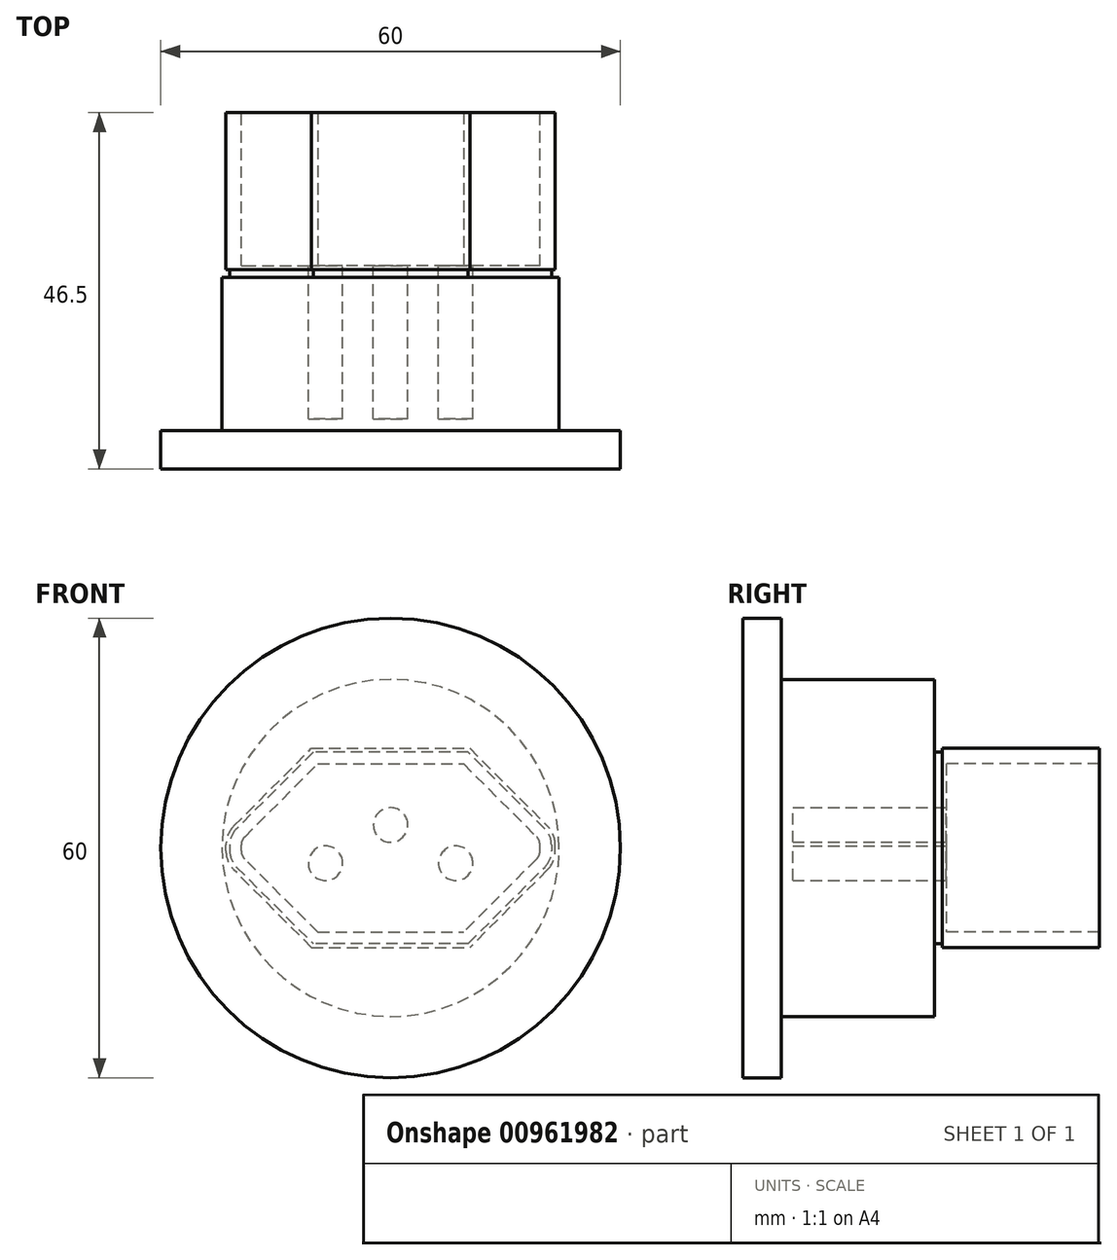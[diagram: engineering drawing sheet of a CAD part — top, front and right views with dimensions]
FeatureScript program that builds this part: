
annotation { "Feature Type Name" : "Feature", "Feature Type Description" : "" }
export const myFeature = defineFeature(function(context is Context, id is Id, definition is map)
    precondition{}
    {
        {
            var Q0;
            Q0=qCreatedBy(makeId("Front.planeOp"),FACE);
            var sketch = newSketch(context, id + "F0", { "sketchPlane" : qUnion([Q0])});
            skLineSegment(sketch, "E0.bottom", {"start": v(19.5, 11) * mm, "end": v(-19.5, 11) * mm});
            skLineSegment(sketch, "E0.top", {"start": v(19.5, -11) * mm, "end": v(-19.5, -11) * mm});
            skLineSegment(sketch, "E0.left", {"start": v(19.5, 11) * mm, "end": v(19.5, -11) * mm});
            skLineSegment(sketch, "E0.right", {"start": v(-19.5, 11) * mm, "end": v(-19.5, -11) * mm});
            skPoint(sketch, "E0.middle", {"position": v(0, 0) * mm});
            skSolve(sketch);
        }
        {
            var Q0;
            Q0=makeQuery(id+"F0.imprint","IMPRINT",FACE,{"disambiguationData":[TD([[makeQuery(id+"F0.imprint","IMPRINT",EDGE,{"derivedFrom":sQuery(id+"F0.wireOp",EDGE,"E0.bottom")}),1.0]])]});
            extrude(context, id + "F1", {"entities" : qUnion([Q0]), "depth" : 20 * mm, "offsetDistance" : 25 * mm});
        }
        {
            var Q0;
            Q0=makeQuery(id+"F1.opExtrude","SWEPT_EDGE",EDGE,{"disambiguationData":[OSD([sQuery(id+"F0.wireOp",EDGE,"E0.bottom"),sQuery(id+"F0.wireOp",EDGE,"E0.left")])]});
            var Q1;
            Q1=makeQuery(id+"F1.opExtrude","SWEPT_EDGE",EDGE,{"disambiguationData":[OSD([sQuery(id+"F0.wireOp",EDGE,"E0.bottom"),sQuery(id+"F0.wireOp",EDGE,"E0.right")])]});
            var Q2;
            Q2=makeQuery(id+"F1.opExtrude","SWEPT_EDGE",EDGE,{"disambiguationData":[OSD([sQuery(id+"F0.wireOp",EDGE,"E0.top"),sQuery(id+"F0.wireOp",EDGE,"E0.left")])]});
            var Q3;
            Q3=makeQuery(id+"F1.opExtrude","SWEPT_EDGE",EDGE,{"disambiguationData":[OSD([sQuery(id+"F0.wireOp",EDGE,"E0.top"),sQuery(id+"F0.wireOp",EDGE,"E0.right")])]});
            chamfer(context, id + "F2", {"entities" : qUnion([Q0, Q1, Q2, Q3]), "width" : 10 * mm, "tangentPropagation" : true});
        }
        {
            var Q0;
            {var subQ0=sQuery(id+"F0.wireOp",EDGE,"E0.left");Q0=makeQuery(id+"F2.opChamfer","BLEND_EDGE",EDGE,{"blendedFrom":[makeQuery(id+"F1.opExtrude","SWEPT_EDGE",EDGE,{"disambiguationData":[OSD([sQuery(id+"F0.wireOp",EDGE,"E0.top"),subQ0])]}),makeQuery(id+"F1.opExtrude","SWEPT_FACE",FACE,{"disambiguationData":[OSD([subQ0])]})],"blendedInto":[makeQuery(id+"F1.opExtrude","SWEPT_FACE",FACE,{"disambiguationData":[OSD([subQ0])]})]});}
            var Q1;
            {var subQ0=sQuery(id+"F0.wireOp",EDGE,"E0.right");Q1=makeQuery(id+"F2.opChamfer","BLEND_EDGE",EDGE,{"blendedFrom":[makeQuery(id+"F1.opExtrude","SWEPT_EDGE",EDGE,{"disambiguationData":[OSD([sQuery(id+"F0.wireOp",EDGE,"E0.bottom"),subQ0])]}),makeQuery(id+"F1.opExtrude","SWEPT_FACE",FACE,{"disambiguationData":[OSD([subQ0])]})],"blendedInto":[makeQuery(id+"F1.opExtrude","SWEPT_FACE",FACE,{"disambiguationData":[OSD([subQ0])]})]});}
            var Q2;
            {var subQ0=sQuery(id+"F0.wireOp",EDGE,"E0.right");Q2=makeQuery(id+"F2.opChamfer","BLEND_EDGE",EDGE,{"blendedFrom":[makeQuery(id+"F1.opExtrude","SWEPT_EDGE",EDGE,{"disambiguationData":[OSD([sQuery(id+"F0.wireOp",EDGE,"E0.top"),subQ0])]}),makeQuery(id+"F1.opExtrude","SWEPT_FACE",FACE,{"disambiguationData":[OSD([subQ0])]})],"blendedInto":[makeQuery(id+"F1.opExtrude","SWEPT_FACE",FACE,{"disambiguationData":[OSD([subQ0])]})]});}
            var Q3;
            {var subQ0=sQuery(id+"F0.wireOp",EDGE,"E0.left");Q3=makeQuery(id+"F2.opChamfer","BLEND_EDGE",EDGE,{"blendedFrom":[makeQuery(id+"F1.opExtrude","SWEPT_EDGE",EDGE,{"disambiguationData":[OSD([sQuery(id+"F0.wireOp",EDGE,"E0.bottom"),subQ0])]}),makeQuery(id+"F1.opExtrude","SWEPT_FACE",FACE,{"disambiguationData":[OSD([subQ0])]})],"blendedInto":[makeQuery(id+"F1.opExtrude","SWEPT_FACE",FACE,{"disambiguationData":[OSD([subQ0])]})]});}
            fillet(context, id + "F3", {"entities" : qUnion([Q0, Q1, Q2, Q3]), "radius" : 1.5 * mm, "tangentPropagation" : true, "allowEdgeOverflow" : false});
        }
        {
            var Q0;
            Q0=makeQuery(id+"F1.opExtrude","CAP_FACE",FACE,{"disambiguationData":[OSD([sQuery(id+"F0.wireOp",EDGE,"E0.bottom"),sQuery(id+"F0.wireOp",EDGE,"E0.top"),sQuery(id+"F0.wireOp",EDGE,"E0.left"),sQuery(id+"F0.wireOp",EDGE,"E0.right")])],"isStart":false});
            var sketch = newSketch(context, id + "F4", { "sketchPlane" : qUnion([Q0])});
            skLineSegment(sketch, "E1.0", {"start": v(-21.5, 0.38) * mm, "end": v(-21.5, -0.38) * mm});
            skArc(sketch, "E1.1", {"start": v(20.47, -2.85) * mm, "mid": v(21.23, -1.72) * mm, "end": v(21.5, -0.38) * mm});
            skLineSegment(sketch, "E1.2", {"start": v(10.33, -13) * mm, "end": v(20.47, -2.85) * mm});
            skLineSegment(sketch, "E1.3", {"start": v(10.33, -13) * mm, "end": v(-10.33, -13) * mm});
            skLineSegment(sketch, "E1.4", {"start": v(-20.47, -2.85) * mm, "end": v(-10.33, -13) * mm});
            skLineSegment(sketch, "E1.5", {"start": v(21.5, 0.38) * mm, "end": v(21.5, -0.38) * mm});
            skArc(sketch, "E1.6", {"start": v(-21.5, -0.38) * mm, "mid": v(-21.23, -1.72) * mm, "end": v(-20.47, -2.85) * mm});
            skArc(sketch, "E1.7", {"start": v(21.5, 0.38) * mm, "mid": v(21.23, 1.72) * mm, "end": v(20.47, 2.85) * mm});
            skLineSegment(sketch, "E1.8", {"start": v(20.47, 2.85) * mm, "end": v(10.33, 13) * mm});
            skLineSegment(sketch, "E1.9", {"start": v(10.33, 13) * mm, "end": v(-10.33, 13) * mm});
            skLineSegment(sketch, "E1.10", {"start": v(-10.33, 13) * mm, "end": v(-20.47, 2.85) * mm});
            skArc(sketch, "E1.11", {"start": v(-20.47, 2.85) * mm, "mid": v(-21.23, 1.72) * mm, "end": v(-21.5, 0.38) * mm});
            skSolve(sketch);
        }
        {
            var Q0;
            Q0 = qSketchRegion(id + "F4", true);
            var Q1;
            Q1=makeQuery(id+"F1.opExtrude","CAP_FACE",FACE,{"disambiguationData":[OSD([sQuery(id+"F0.wireOp",EDGE,"E0.bottom"),sQuery(id+"F0.wireOp",EDGE,"E0.top"),sQuery(id+"F0.wireOp",EDGE,"E0.left"),sQuery(id+"F0.wireOp",EDGE,"E0.right")])],"isStart":true});
            extrude(context, id + "F5", {"entities" : qUnion([Q0]), "operationType" : NewBodyOperationType.ADD, "endBound" : BoundingType.UP_TO_SURFACE, "oppositeDirection" : true, "depth" : 25 * mm, "endBoundEntityFace" : qUnion([Q1]), "offsetDistance" : 25 * mm});
        }
        {
            var Q0;
            Q0=makeQuery(id+"F1.opExtrude","CAP_FACE",FACE,{"disambiguationData":[OSD([sQuery(id+"F0.wireOp",EDGE,"E0.bottom"),sQuery(id+"F0.wireOp",EDGE,"E0.top"),sQuery(id+"F0.wireOp",EDGE,"E0.left"),sQuery(id+"F0.wireOp",EDGE,"E0.right")])],"isStart":false});
            var Q1;
            Q1=makeQuery(id+"F1.opExtrude","CAP_FACE",FACE,{"disambiguationData":[OSD([sQuery(id+"F0.wireOp",EDGE,"E0.bottom"),sQuery(id+"F0.wireOp",EDGE,"E0.top"),sQuery(id+"F0.wireOp",EDGE,"E0.left"),sQuery(id+"F0.wireOp",EDGE,"E0.right")])],"isStart":true});
            shell(context, id + "F6", {"entities" : qUnion([Q0, Q1]), "thickness" : 2 * mm});
        }
        {
            var Q0;
            Q0=makeQuery(id+"F5.boolean.opBoolean","MERGE",FACE,{"derivedFrom":[makeQuery(id+"F1.opExtrude","CAP_FACE",FACE,{"disambiguationData":[OSD([sQuery(id+"F0.wireOp",EDGE,"E0.bottom"),sQuery(id+"F0.wireOp",EDGE,"E0.top"),sQuery(id+"F0.wireOp",EDGE,"E0.left"),sQuery(id+"F0.wireOp",EDGE,"E0.right")])],"isStart":false}),makeQuery(id+"F5.opExtrude","CAP_FACE",FACE,{"disambiguationData":[OSD([sQuery(id+"F4.wireOp",EDGE,"E1.0"),sQuery(id+"F4.wireOp",EDGE,"E1.1"),sQuery(id+"F4.wireOp",EDGE,"E1.2"),sQuery(id+"F4.wireOp",EDGE,"E1.3"),sQuery(id+"F4.wireOp",EDGE,"E1.4"),sQuery(id+"F4.wireOp",EDGE,"E1.5"),sQuery(id+"F4.wireOp",EDGE,"E1.6"),sQuery(id+"F4.wireOp",EDGE,"E1.7"),sQuery(id+"F4.wireOp",EDGE,"E1.8"),sQuery(id+"F4.wireOp",EDGE,"E1.9"),sQuery(id+"F4.wireOp",EDGE,"E1.10"),sQuery(id+"F4.wireOp",EDGE,"E1.11")])],"isStart":true})]});
            var sketch = newSketch(context, id + "F7", { "sketchPlane" : qUnion([Q0])});
            skCircle(sketch, "E2", {"center": v(-8.5, -2) * mm, "radius": 2.25 * mm});
            skLineSegment(sketch, "E3", {"start": v(-8.5, -2) * mm, "end": v(8.5, -2) * mm, "construction": true});
            skCircle(sketch, "E4", {"center": v(8.5, -2) * mm, "radius": 2.25 * mm});
            skCircle(sketch, "E5", {"center": v(0, 3) * mm, "radius": 2.25 * mm});
            skLineSegment(sketch, "E6.0", {"start": v(-10.33, 13) * mm, "end": v(-20.47, 2.85) * mm});
            skLineSegment(sketch, "E7.0", {"start": v(10.33, 13) * mm, "end": v(-10.33, 13) * mm});
            skLineSegment(sketch, "E8.0", {"start": v(20.47, 2.85) * mm, "end": v(10.33, 13) * mm});
            skArc(sketch, "E9.0", {"start": v(21.5, 0.38) * mm, "mid": v(21.23, 1.72) * mm, "end": v(20.47, 2.85) * mm});
            skLineSegment(sketch, "E10.0", {"start": v(21.5, 0.38) * mm, "end": v(21.5, -0.38) * mm});
            skArc(sketch, "E11.0", {"start": v(20.47, -2.85) * mm, "mid": v(21.23, -1.72) * mm, "end": v(21.5, -0.38) * mm});
            skLineSegment(sketch, "E12.0", {"start": v(10.33, -13) * mm, "end": v(20.47, -2.85) * mm});
            skLineSegment(sketch, "E13.0", {"start": v(10.33, -13) * mm, "end": v(-10.33, -13) * mm});
            skLineSegment(sketch, "E14.0", {"start": v(-20.47, -2.85) * mm, "end": v(-10.33, -13) * mm});
            skArc(sketch, "E15.0", {"start": v(-21.5, -0.38) * mm, "mid": v(-21.23, -1.72) * mm, "end": v(-20.47, -2.85) * mm});
            skLineSegment(sketch, "E16.0", {"start": v(-21.5, 0.38) * mm, "end": v(-21.5, -0.38) * mm});
            skArc(sketch, "E17.0", {"start": v(-20.47, 2.85) * mm, "mid": v(-21.23, 1.72) * mm, "end": v(-21.5, 0.38) * mm});
            skSolve(sketch);
        }
        {
            var Q0;
            Q0 = qSketchRegion(id + "F7", true);
            extrude(context, id + "F8", {"entities" : qUnion([Q0]), "operationType" : NewBodyOperationType.ADD, "depth" : 1.5 * mm, "offsetDistance" : 25 * mm});
        }
        {
            var Q0;
            Q0=makeQuery(id+"F8.opExtrude","CAP_FACE",FACE,{"disambiguationData":[OSD([sQuery(id+"F7.wireOp",EDGE,"E2"),sQuery(id+"F7.wireOp",EDGE,"E4"),sQuery(id+"F7.wireOp",EDGE,"E5"),sQuery(id+"F7.wireOp",EDGE,"E6.0"),sQuery(id+"F7.wireOp",EDGE,"E7.0"),sQuery(id+"F7.wireOp",EDGE,"E8.0"),sQuery(id+"F7.wireOp",EDGE,"E9.0"),sQuery(id+"F7.wireOp",EDGE,"E10.0"),sQuery(id+"F7.wireOp",EDGE,"E11.0"),sQuery(id+"F7.wireOp",EDGE,"E12.0"),sQuery(id+"F7.wireOp",EDGE,"E13.0"),sQuery(id+"F7.wireOp",EDGE,"E14.0"),sQuery(id+"F7.wireOp",EDGE,"E15.0"),sQuery(id+"F7.wireOp",EDGE,"E16.0"),sQuery(id+"F7.wireOp",EDGE,"E17.0")])],"isStart":false});
            cPlane(context, id + "F9", {"entities" : qUnion([Q0]), "cplaneType" : CPlaneType.OFFSET, "offset" : 0 * mm, "width" : 150 * mm, "height" : 150 * mm});
        }
        {
            var Q0;
            Q0=makeQuery(id+"F8.opExtrude","CAP_FACE",FACE,{"disambiguationData":[OSD([sQuery(id+"F7.wireOp",EDGE,"E2"),sQuery(id+"F7.wireOp",EDGE,"E4"),sQuery(id+"F7.wireOp",EDGE,"E5"),sQuery(id+"F7.wireOp",EDGE,"E6.0"),sQuery(id+"F7.wireOp",EDGE,"E7.0"),sQuery(id+"F7.wireOp",EDGE,"E8.0"),sQuery(id+"F7.wireOp",EDGE,"E9.0"),sQuery(id+"F7.wireOp",EDGE,"E10.0"),sQuery(id+"F7.wireOp",EDGE,"E11.0"),sQuery(id+"F7.wireOp",EDGE,"E12.0"),sQuery(id+"F7.wireOp",EDGE,"E13.0"),sQuery(id+"F7.wireOp",EDGE,"E14.0"),sQuery(id+"F7.wireOp",EDGE,"E15.0"),sQuery(id+"F7.wireOp",EDGE,"E16.0"),sQuery(id+"F7.wireOp",EDGE,"E17.0")])],"isStart":false});
            var sketch = newSketch(context, id + "F10", { "sketchPlane" : qUnion([Q0])});
            skCircle(sketch, "E18", {"center": v(0, 0) * mm, "radius": 27.5 * mm});
            skSolve(sketch);
        }
        {
            var Q0;
            Q0=makeQuery(id+"F10.imprint","IMPRINT",FACE,{"disambiguationData":[TD([[makeQuery(id+"F10.imprint","IMPRINT",EDGE,{"derivedFrom":makeQuery(id+"F8.opExtrude","CAP_EDGE",EDGE,{"disambiguationData":[OSD([sQuery(id+"F7.wireOp",EDGE,"E2")])],"isStart":false})}),-1.0]])]});
            extrude(context, id + "F11", {"entities" : qUnion([Q0]), "operationType" : NewBodyOperationType.ADD, "depth" : 20 * mm, "offsetDistance" : 25 * mm});
        }
        {
            var Q0;
            Q0=qCreatedBy(id+"F9.planeOp",FACE);
            var sketch = newSketch(context, id + "F12", { "sketchPlane" : qUnion([Q0])});
            skLineSegment(sketch, "E19.0", {"start": v(10.33, 13) * mm, "end": v(-10.33, 13) * mm});
            skLineSegment(sketch, "E20.0", {"start": v(-10.33, 13) * mm, "end": v(-20.47, 2.85) * mm});
            skArc(sketch, "E21.0", {"start": v(-20.47, 2.85) * mm, "mid": v(-21.23, 1.72) * mm, "end": v(-21.5, 0.38) * mm});
            skLineSegment(sketch, "E22.0", {"start": v(-21.5, 0.38) * mm, "end": v(-21.5, -0.38) * mm});
            skArc(sketch, "E23.0", {"start": v(-21.5, -0.38) * mm, "mid": v(-21.23, -1.72) * mm, "end": v(-20.47, -2.85) * mm});
            skLineSegment(sketch, "E24.0", {"start": v(-20.47, -2.85) * mm, "end": v(-10.33, -13) * mm});
            skLineSegment(sketch, "E25.0", {"start": v(10.33, -13) * mm, "end": v(-10.33, -13) * mm});
            skLineSegment(sketch, "E26.0", {"start": v(10.33, -13) * mm, "end": v(20.47, -2.85) * mm});
            skArc(sketch, "E27.0", {"start": v(20.47, -2.85) * mm, "mid": v(21.23, -1.72) * mm, "end": v(21.5, -0.38) * mm});
            skLineSegment(sketch, "E28.0", {"start": v(21.5, 0.38) * mm, "end": v(21.5, -0.38) * mm});
            skArc(sketch, "E29.0", {"start": v(21.5, 0.38) * mm, "mid": v(21.23, 1.72) * mm, "end": v(20.47, 2.85) * mm});
            skLineSegment(sketch, "E30.0", {"start": v(20.47, 2.85) * mm, "end": v(10.33, 13) * mm});
            skLineSegment(sketch, "E31.0", {"start": v(10.12, 12.5) * mm, "end": v(-10.12, 12.5) * mm});
            skLineSegment(sketch, "E31.1", {"start": v(-20.12, -2.5) * mm, "end": v(-10.12, -12.5) * mm});
            skArc(sketch, "E31.2", {"start": v(-21, -0.38) * mm, "mid": v(-20.77, -1.53) * mm, "end": v(-20.12, -2.5) * mm});
            skLineSegment(sketch, "E31.3", {"start": v(-21, 0.38) * mm, "end": v(-21, -0.38) * mm});
            skArc(sketch, "E31.4", {"start": v(-20.12, 2.5) * mm, "mid": v(-20.77, 1.53) * mm, "end": v(-21, 0.38) * mm});
            skLineSegment(sketch, "E31.5", {"start": v(10.12, -12.5) * mm, "end": v(-10.12, -12.5) * mm});
            skLineSegment(sketch, "E31.6", {"start": v(-10.12, 12.5) * mm, "end": v(-20.12, 2.5) * mm});
            skLineSegment(sketch, "E31.7", {"start": v(10.12, -12.5) * mm, "end": v(20.12, -2.5) * mm});
            skArc(sketch, "E31.8", {"start": v(20.12, -2.5) * mm, "mid": v(20.77, -1.53) * mm, "end": v(21, -0.38) * mm});
            skLineSegment(sketch, "E31.9", {"start": v(21, 0.38) * mm, "end": v(21, -0.38) * mm});
            skArc(sketch, "E31.10", {"start": v(21, 0.38) * mm, "mid": v(20.77, 1.53) * mm, "end": v(20.12, 2.5) * mm});
            skLineSegment(sketch, "E31.11", {"start": v(20.12, 2.5) * mm, "end": v(10.12, 12.5) * mm});
            skSolve(sketch);
        }
        {
            var Q0;
            Q0 = qSketchRegion(id + "F12", true);
            extrude(context, id + "F13", {"entities" : qUnion([Q0]), "operationType" : NewBodyOperationType.REMOVE, "oppositeDirection" : true, "depth" : 1 * mm, "offsetDistance" : 25 * mm});
        }
        {
            var Q0;
            Q0=makeQuery(id+"F11.opExtrude","CAP_FACE",FACE,{"disambiguationData":[OSD([sQuery(id+"F7.wireOp",EDGE,"E2"),sQuery(id+"F7.wireOp",EDGE,"E4"),sQuery(id+"F7.wireOp",EDGE,"E5"),sQuery(id+"F7.wireOp",EDGE,"E6.0"),sQuery(id+"F7.wireOp",EDGE,"E7.0"),sQuery(id+"F7.wireOp",EDGE,"E8.0"),sQuery(id+"F7.wireOp",EDGE,"E9.0"),sQuery(id+"F7.wireOp",EDGE,"E10.0"),sQuery(id+"F7.wireOp",EDGE,"E11.0"),sQuery(id+"F7.wireOp",EDGE,"E12.0"),sQuery(id+"F7.wireOp",EDGE,"E13.0"),sQuery(id+"F7.wireOp",EDGE,"E14.0"),sQuery(id+"F7.wireOp",EDGE,"E15.0"),sQuery(id+"F7.wireOp",EDGE,"E16.0"),sQuery(id+"F7.wireOp",EDGE,"E17.0")])],"isStart":false});
            var sketch = newSketch(context, id + "F14", { "sketchPlane" : qUnion([Q0])});
            skCircle(sketch, "E32", {"center": v(0, 0) * mm, "radius": 30 * mm});
            skSolve(sketch);
        }
        {
            var Q0;
            Q0 = qSketchRegion(id + "F14", true);
            extrude(context, id + "F15", {"entities" : qUnion([Q0]), "operationType" : NewBodyOperationType.ADD, "depth" : 5 * mm, "offsetDistance" : 25 * mm});
        }
        {
            var Q0;
            {var subQ12=sQuery(id+"F14.wireOp",EDGE,"E32");Q0=makeQuery(id+"F15.boolean.opBoolean","SPLIT",FACE,{"disambiguationData":[TD([makeQuery(id+"F5.opExtrude","SWEPT_FACE",FACE,{"disambiguationData":[OSD([sQuery(id+"F4.wireOp",EDGE,"E1.0")])]})])],"derivedFrom":makeQuery(id+"F15.opExtrude","CAP_FACE",FACE,{"disambiguationData":[OSD([subQ12])],"isStart":true})});}
            var sketch = newSketch(context, id + "F16", { "sketchPlane" : qUnion([Q0])});
            skCircle(sketch, "E33", {"center": v(0, 0) * mm, "radius": 22 * mm});
            skSolve(sketch);
        }
        {
            var Q0;
            Q0 = qSketchRegion(id + "F16", true);
            var Q1;
            Q1=makeQuery(id+"F13.boolean.opBoolean","COPY",FACE,{"derivedFrom":makeQuery(id+"F13.opExtrude","CAP_FACE",FACE,{"disambiguationData":[OSD([sQuery(id+"F12.wireOp",EDGE,"E19.0"),sQuery(id+"F12.wireOp",EDGE,"E20.0"),sQuery(id+"F12.wireOp",EDGE,"E21.0"),sQuery(id+"F12.wireOp",EDGE,"E22.0"),sQuery(id+"F12.wireOp",EDGE,"E23.0"),sQuery(id+"F12.wireOp",EDGE,"E24.0"),sQuery(id+"F12.wireOp",EDGE,"E25.0"),sQuery(id+"F12.wireOp",EDGE,"E26.0"),sQuery(id+"F12.wireOp",EDGE,"E27.0"),sQuery(id+"F12.wireOp",EDGE,"E28.0"),sQuery(id+"F12.wireOp",EDGE,"E29.0"),sQuery(id+"F12.wireOp",EDGE,"E30.0"),sQuery(id+"F12.wireOp",EDGE,"E31.0"),sQuery(id+"F12.wireOp",EDGE,"E31.1"),sQuery(id+"F12.wireOp",EDGE,"E31.2"),sQuery(id+"F12.wireOp",EDGE,"E31.3"),sQuery(id+"F12.wireOp",EDGE,"E31.4"),sQuery(id+"F12.wireOp",EDGE,"E31.5"),sQuery(id+"F12.wireOp",EDGE,"E31.6"),sQuery(id+"F12.wireOp",EDGE,"E31.7"),sQuery(id+"F12.wireOp",EDGE,"E31.8"),sQuery(id+"F12.wireOp",EDGE,"E31.9"),sQuery(id+"F12.wireOp",EDGE,"E31.10"),sQuery(id+"F12.wireOp",EDGE,"E31.11")])],"isStart":true})});
            extrude(context, id + "F17", {"entities" : qUnion([Q0]), "operationType" : NewBodyOperationType.ADD, "endBound" : BoundingType.UP_TO_SURFACE, "depth" : 25 * mm, "endBoundEntityFace" : qUnion([Q1]), "offsetDistance" : 25 * mm});
        }
        {
            var Q0;
            Q0=makeQuery(id+"F8.opExtrude","CAP_FACE",FACE,{"disambiguationData":[OSD([sQuery(id+"F7.wireOp",EDGE,"E2"),sQuery(id+"F7.wireOp",EDGE,"E4"),sQuery(id+"F7.wireOp",EDGE,"E5"),sQuery(id+"F7.wireOp",EDGE,"E6.0"),sQuery(id+"F7.wireOp",EDGE,"E7.0"),sQuery(id+"F7.wireOp",EDGE,"E8.0"),sQuery(id+"F7.wireOp",EDGE,"E9.0"),sQuery(id+"F7.wireOp",EDGE,"E10.0"),sQuery(id+"F7.wireOp",EDGE,"E11.0"),sQuery(id+"F7.wireOp",EDGE,"E12.0"),sQuery(id+"F7.wireOp",EDGE,"E13.0"),sQuery(id+"F7.wireOp",EDGE,"E14.0"),sQuery(id+"F7.wireOp",EDGE,"E15.0"),sQuery(id+"F7.wireOp",EDGE,"E16.0"),sQuery(id+"F7.wireOp",EDGE,"E17.0")])],"isStart":true});
            var sketch = newSketch(context, id + "F18", { "sketchPlane" : qUnion([Q0])});
            skCircle(sketch, "E34.0", {"center": v(8.5, -2) * mm, "radius": 2.25 * mm});
            skCircle(sketch, "E35.0", {"center": v(0, 3) * mm, "radius": 2.25 * mm});
            skCircle(sketch, "E36.0", {"center": v(-8.5, -2) * mm, "radius": 2.25 * mm});
            skSolve(sketch);
        }
        {
            var Q0;
            Q0 = qSketchRegion(id + "F18", true);
            extrude(context, id + "F19", {"entities" : qUnion([Q0]), "operationType" : NewBodyOperationType.REMOVE, "oppositeDirection" : true, "depth" : 20 * mm, "offsetDistance" : 25 * mm});
        }
    });
